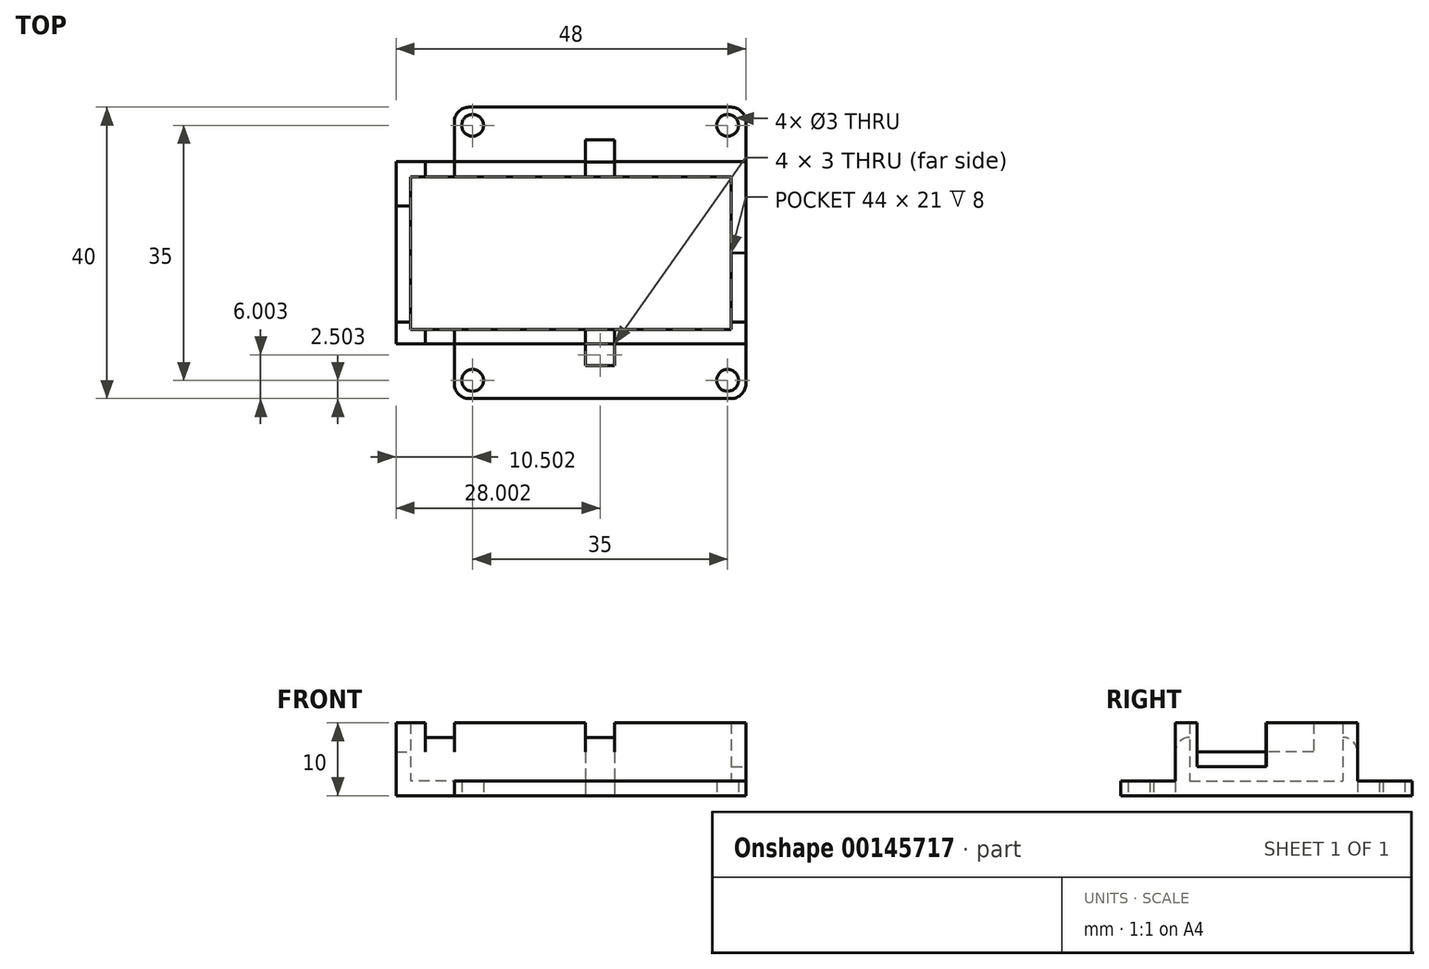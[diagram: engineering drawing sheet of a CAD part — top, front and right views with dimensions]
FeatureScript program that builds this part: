
annotation { "Feature Type Name" : "Feature", "Feature Type Description" : "" }
export const myFeature = defineFeature(function(context is Context, id is Id, definition is map)
    precondition{}
    {
        {
            var Q0;
            Q0=qCreatedBy(makeId("Top.planeOp"),FACE);
            var sketch = newSketch(context, id + "F0", { "sketchPlane" : qUnion([Q0])});
            skLineSegment(sketch, "E0.bottom", {"start": v(0.1, -19.97) * mm, "end": v(-19.9, -19.97) * mm});
            skLineSegment(sketch, "E0.top", {"start": v(0.1, 0.03) * mm, "end": v(-19.9, 0.03) * mm});
            skLineSegment(sketch, "E0.left", {"start": v(0.1, -19.97) * mm, "end": v(0.1, 0.03) * mm});
            skLineSegment(sketch, "E0.right", {"start": v(-19.9, -19.97) * mm, "end": v(-19.9, 0.03) * mm});
            skPoint(sketch, "E1", {"position": v(-17.4, -17.47) * mm});
            skLineSegment(sketch, "E2.bottom", {"start": v(-1.9, -12.47) * mm, "end": v(0.1, -12.47) * mm});
            skLineSegment(sketch, "E2.top", {"start": v(-1.9, -15.47) * mm, "end": v(0.1, -15.47) * mm});
            skLineSegment(sketch, "E2.left", {"start": v(0.1, -12.47) * mm, "end": v(0.1, -15.47) * mm});
            skLineSegment(sketch, "E2.right", {"start": v(-1.9, -12.47) * mm, "end": v(-1.9, -15.47) * mm});
            skSolve(sketch);
        }
        {
            var Q0;
            Q0=makeQuery(id+"F0.imprint","IMPRINT",FACE,{"disambiguationData":[TD([[makeQuery(id+"F0.imprint","IMPRINT",EDGE,{"derivedFrom":sQuery(id+"F0.wireOp",EDGE,"E0.bottom")}),-1.0]])]});
            extrude(context, id + "F1", {"entities" : qUnion([Q0]), "depth" : 2 * mm});
        }
        {
            var Q0;
            Q0=makeQuery(id+"F1.opExtrude","SWEPT_EDGE",EDGE,{"disambiguationData":[OSD([sQuery(id+"F0.wireOp",EDGE,"E0.bottom"),sQuery(id+"F0.wireOp",EDGE,"E0.right")])]});
            fillet(context, id + "F2", {"entities" : qUnion([Q0]), "radius" : 2 * mm, "tangentPropagation" : true, "allowEdgeOverflow" : false});
        }
        {
            var Q0;
            Q0=sQuery(id+"F0.wireOp",VERTEX,"E1");
            var Q1;
            Q1=makeQuery(id+"F1.opExtrude","SWEPT_BODY",BODY,{"disambiguationData":[OSD([sQuery(id+"F0.wireOp",EDGE,"E0.bottom"),sQuery(id+"F0.wireOp",EDGE,"E0.top"),sQuery(id+"F0.wireOp",EDGE,"E0.left"),sQuery(id+"F0.wireOp",EDGE,"E0.right")])]});
            hole(context, id + "F3", {"style" : HoleStyle.SIMPLE, "endStyle" : HoleEndStyle.THROUGH, "oppositeDirection" : true, "holeDiameter" : 3 * mm, "locations" : qUnion([Q0]), "scope" : qUnion([Q1]), "isTappedThrough" : true});
        }
        {
            var Q0;
            Q0=makeQuery(id+"F1.opExtrude","SWEPT_BODY",BODY,{"disambiguationData":[OSD([sQuery(id+"F0.wireOp",EDGE,"E0.bottom"),sQuery(id+"F0.wireOp",EDGE,"E0.top"),sQuery(id+"F0.wireOp",EDGE,"E0.left"),sQuery(id+"F0.wireOp",EDGE,"E0.right")])]});
            var Q1;
            Q1=makeQuery(id+"F1.opExtrude","SWEPT_FACE",FACE,{"disambiguationData":[OSD([sQuery(id+"F0.wireOp",EDGE,"E0.left")])]});
            mirror(context, id + "F4", {"operationType" : NewBodyOperationType.ADD, "entities" : qUnion([Q0]), "mirrorPlane" : qUnion([Q1])});
        }
        {
            var Q0;
            Q0=makeQuery(id+"F1.opExtrude","SWEPT_BODY",BODY,{"disambiguationData":[OSD([sQuery(id+"F0.wireOp",EDGE,"E0.bottom"),sQuery(id+"F0.wireOp",EDGE,"E0.top"),sQuery(id+"F0.wireOp",EDGE,"E0.left"),sQuery(id+"F0.wireOp",EDGE,"E0.right")])]});
            var Q1;
            {var subQ0=makeQuery(id+"F1.opExtrude","SWEPT_FACE",FACE,{"disambiguationData":[OSD([sQuery(id+"F0.wireOp",EDGE,"E0.top")])]});Q1=makeQuery(id+"F4.boolean.opBoolean","MERGE",FACE,{"derivedFrom":[subQ0,makeQuery(id+"F4.opPattern","COPY",FACE,{"derivedFrom":subQ0,"instanceName":"1"})]});}
            mirror(context, id + "F5", {"operationType" : NewBodyOperationType.ADD, "entities" : qUnion([Q0]), "mirrorPlane" : qUnion([Q1])});
        }
        {
            var Q0;
            {var subQ0=makeQuery(id+"F1.opExtrude","CAP_FACE",FACE,{"disambiguationData":[OSD([sQuery(id+"F0.wireOp",EDGE,"E0.bottom"),sQuery(id+"F0.wireOp",EDGE,"E0.top"),sQuery(id+"F0.wireOp",EDGE,"E0.left"),sQuery(id+"F0.wireOp",EDGE,"E0.right")])],"isStart":true});var subQ1=makeQuery(id+"F4.boolean.opBoolean","MERGE",FACE,{"derivedFrom":[subQ0,makeQuery(id+"F4.opPattern","COPY",FACE,{"derivedFrom":subQ0,"instanceName":"1"})]});Q0=makeQuery(id+"F5.boolean.opBoolean","MERGE",FACE,{"derivedFrom":[subQ1,makeQuery(id+"F5.opPattern","COPY",FACE,{"derivedFrom":subQ1,"instanceName":"1"})]});}
            var sketch = newSketch(context, id + "F6", { "sketchPlane" : qUnion([Q0])});
            skLineSegment(sketch, "E3.bottom", {"start": v(20.1, -12.55) * mm, "end": v(-27.9, -12.55) * mm});
            skLineSegment(sketch, "E3.top", {"start": v(20.1, 12.45) * mm, "end": v(-27.9, 12.45) * mm});
            skLineSegment(sketch, "E3.left", {"start": v(20.1, -12.55) * mm, "end": v(20.1, 12.45) * mm});
            skLineSegment(sketch, "E3.right", {"start": v(-27.9, -12.55) * mm, "end": v(-27.9, 12.45) * mm});
            skLineSegment(sketch, "E4.bottom", {"start": v(18.1, -10.5) * mm, "end": v(-25.9, -10.5) * mm});
            skLineSegment(sketch, "E4.top", {"start": v(18.1, 10.5) * mm, "end": v(-25.9, 10.5) * mm});
            skLineSegment(sketch, "E4.left", {"start": v(18.1, -10.5) * mm, "end": v(18.1, 10.5) * mm});
            skLineSegment(sketch, "E4.right", {"start": v(-25.9, -10.5) * mm, "end": v(-25.9, 10.5) * mm});
            skLineSegment(sketch, "E5", {"start": v(-27.9, -6.5) * mm, "end": v(-25.9, -6.5) * mm});
            skLineSegment(sketch, "E6", {"start": v(-27.9, 9.5) * mm, "end": v(-25.9, 9.5) * mm});
            skLineSegment(sketch, "E7", {"start": v(18.1, 0) * mm, "end": v(20.1, -0.05) * mm});
            skLineSegment(sketch, "E8", {"start": v(18.1, 9.5) * mm, "end": v(20.1, 9.5) * mm});
            skLineSegment(sketch, "E9", {"start": v(-1.9, -12.53) * mm, "end": v(-1.9, -10.5) * mm});
            skLineSegment(sketch, "E10", {"start": v(2.1, -12.53) * mm, "end": v(2.1, -10.5) * mm});
            skLineSegment(sketch, "E11", {"start": v(-1.9, 12.47) * mm, "end": v(-1.9, 10.5) * mm});
            skLineSegment(sketch, "E12", {"start": v(2.1, 12.47) * mm, "end": v(2.1, 10.5) * mm});
            skLineSegment(sketch, "E13", {"start": v(-23.9, 12.45) * mm, "end": v(-23.9, 10.5) * mm});
            skLineSegment(sketch, "E14", {"start": v(-23.9, -10.5) * mm, "end": v(-23.9, -12.55) * mm});
            skSolve(sketch);
        }
        {
            var Q0;
            {var subQ0=sQuery(id+"F6.wireOp",EDGE,"E4.right");var subQ3=sQuery(id+"F6.wireOp",EDGE,"E4.bottom");var subQ4=makeQuery(id+"F6.imprint","INTERSECT",VERTEX,{"derivedFrom":[subQ3,subQ0]});Q0=makeQuery(id+"F6.imprint","IMPRINT",FACE,{"disambiguationData":[TD([[makeQuery(id+"F6.imprint","IMPRINT",EDGE,{"disambiguationData":[TD([[subQ4,-1.0]])],"derivedFrom":subQ0}),-1.0]])]});}
            var Q1;
            {var subQ0=sQuery(id+"F6.wireOp",EDGE,"E7");Q1=makeQuery(id+"F6.imprint","IMPRINT",FACE,{"disambiguationData":[TD([[makeQuery(id+"F6.imprint","IMPRINT",EDGE,{"derivedFrom":subQ0}),1.0]])]});}
            var Q2;
            {var subQ7=sQuery(id+"F6.wireOp",EDGE,"E4.bottom");var subQ9=sQuery(id+"F6.wireOp",EDGE,"E4.left");var subQ13=makeQuery(id+"F6.imprint","INTERSECT",VERTEX,{"derivedFrom":[subQ7,subQ9]});Q2=makeQuery(id+"F6.imprint","IMPRINT",FACE,{"disambiguationData":[TD([[makeQuery(id+"F6.imprint","IMPRINT",EDGE,{"disambiguationData":[TD([[subQ13,-1.0]])],"derivedFrom":subQ7}),-1.0]])]});}
            extrude(context, id + "F7", {"entities" : qUnion([Q0, Q1, Q2]), "operationType" : NewBodyOperationType.ADD, "oppositeDirection" : true, "depth" : 2 * mm});
        }
        {
            var Q0;
            {var subQ0=sQuery(id+"F6.wireOp",EDGE,"E13");Q0=makeQuery(id+"F6.imprint","IMPRINT",FACE,{"disambiguationData":[TD([[makeQuery(id+"F6.imprint","IMPRINT",EDGE,{"derivedFrom":subQ0}),1.0]])]});}
            var Q1;
            {var subQ0=sQuery(id+"F6.wireOp",EDGE,"E14");Q1=makeQuery(id+"F6.imprint","IMPRINT",FACE,{"disambiguationData":[TD([[makeQuery(id+"F6.imprint","IMPRINT",EDGE,{"derivedFrom":subQ0}),1.0]])]});}
            var Q2;
            {var subQ0=sQuery(id+"F6.wireOp",EDGE,"E9");Q2=makeQuery(id+"F6.imprint","IMPRINT",FACE,{"disambiguationData":[TD([[makeQuery(id+"F6.imprint","IMPRINT",EDGE,{"derivedFrom":subQ0}),-1.0]])]});}
            var Q3;
            {var subQ0=sQuery(id+"F6.wireOp",EDGE,"E12");var subQ1=sQuery(id+"F6.wireOp",EDGE,"E3.top");var subQ2=makeQuery(id+"F6.imprint","INTERSECT",VERTEX,{"derivedFrom":[subQ1,subQ0]});Q3=makeQuery(id+"F6.imprint","IMPRINT",FACE,{"disambiguationData":[TD([[makeQuery(id+"F6.imprint","IMPRINT",EDGE,{"disambiguationData":[TD([[subQ2,-1.0]])],"derivedFrom":subQ1}),1.0]])]});}
            extrude(context, id + "F8", {"entities" : qUnion([Q0, Q1, Q2, Q3]), "operationType" : NewBodyOperationType.ADD, "oppositeDirection" : true, "depth" : 8 * mm});
        }
        {
            var Q0;
            {var subQ3=sQuery(id+"F6.wireOp",EDGE,"E5");Q0=makeQuery(id+"F6.imprint","IMPRINT",FACE,{"disambiguationData":[TD([[makeQuery(id+"F6.imprint","IMPRINT",EDGE,{"derivedFrom":subQ3}),-1.0]])]});}
            var Q1;
            {var subQ3=sQuery(id+"F6.wireOp",EDGE,"E6");Q1=makeQuery(id+"F6.imprint","IMPRINT",FACE,{"disambiguationData":[TD([[makeQuery(id+"F6.imprint","IMPRINT",EDGE,{"derivedFrom":subQ3}),1.0]])]});}
            var Q2;
            {var subQ0=sQuery(id+"F6.wireOp",EDGE,"E9");var subQ6=sQuery(id+"F6.wireOp",EDGE,"E4.bottom");var subQ7=makeQuery(id+"F6.imprint","INTERSECT",VERTEX,{"derivedFrom":[subQ6,subQ0]});Q2=makeQuery(id+"F6.imprint","IMPRINT",FACE,{"disambiguationData":[TD([[makeQuery(id+"F6.imprint","IMPRINT",EDGE,{"disambiguationData":[TD([[subQ7,1.0]])],"derivedFrom":subQ0}),1.0]])]});}
            var Q3;
            {var subQ3=sQuery(id+"F6.wireOp",EDGE,"E7");Q3=makeQuery(id+"F6.imprint","IMPRINT",FACE,{"disambiguationData":[TD([[makeQuery(id+"F6.imprint","IMPRINT",EDGE,{"derivedFrom":subQ3}),-1.0]])]});}
            var Q4;
            {var subQ3=sQuery(id+"F6.wireOp",EDGE,"E8");Q4=makeQuery(id+"F6.imprint","IMPRINT",FACE,{"disambiguationData":[TD([[makeQuery(id+"F6.imprint","IMPRINT",EDGE,{"derivedFrom":subQ3}),1.0]])]});}
            var Q5;
            {var subQ0=sQuery(id+"F6.wireOp",EDGE,"E11");var subQ6=sQuery(id+"F6.wireOp",EDGE,"E4.top");var subQ7=makeQuery(id+"F6.imprint","INTERSECT",VERTEX,{"derivedFrom":[subQ6,subQ0]});Q5=makeQuery(id+"F6.imprint","IMPRINT",FACE,{"disambiguationData":[TD([[makeQuery(id+"F6.imprint","IMPRINT",EDGE,{"disambiguationData":[TD([[subQ7,1.0]])],"derivedFrom":subQ0}),-1.0]])]});}
            extrude(context, id + "F9", {"entities" : qUnion([Q0, Q1, Q2, Q3, Q4, Q5]), "operationType" : NewBodyOperationType.ADD, "oppositeDirection" : true, "depth" : 10 * mm});
        }
        {
            var Q0;
            Q0=makeQuery(id+"F8.opExtrude","CAP_EDGE",EDGE,{"disambiguationData":[OSD([sQuery(id+"F0.wireOp",EDGE,"E2.bottom")])],"isStart":false});
            var Q1;
            Q1=makeQuery(id+"F8.opExtrude","CAP_EDGE",EDGE,{"disambiguationData":[OSD([sQuery(id+"F6.wireOp",EDGE,"E3.bottom")])],"isStart":false});
            var Q2;
            Q2=makeQuery(id+"F8.opExtrude","CAP_EDGE",EDGE,{"disambiguationData":[OSD([sQuery(id+"F6.wireOp",EDGE,"E3.top")])],"isStart":false});
            fillet(context, id + "F10", {"entities" : qUnion([Q0, Q1, Q2]), "radius" : 2 * mm, "tangentPropagation" : true, "allowEdgeOverflow" : false});
        }
        {
            var Q0;
            {var subQ0=sQuery(id+"F6.wireOp",EDGE,"E7");Q0=makeQuery(id+"F6.imprint","IMPRINT",FACE,{"disambiguationData":[TD([[makeQuery(id+"F6.imprint","IMPRINT",EDGE,{"derivedFrom":subQ0}),1.0]])]});}
            extrude(context, id + "F11", {"entities" : qUnion([Q0]), "operationType" : NewBodyOperationType.ADD, "oppositeDirection" : true, "depth" : 4 * mm});
        }
        {
            var Q0;
            {var subQ0=sQuery(id+"F6.wireOp",EDGE,"E5");Q0=makeQuery(id+"F6.imprint","IMPRINT",FACE,{"disambiguationData":[TD([[makeQuery(id+"F6.imprint","IMPRINT",EDGE,{"derivedFrom":subQ0}),1.0]])]});}
            extrude(context, id + "F12", {"entities" : qUnion([Q0]), "operationType" : NewBodyOperationType.ADD, "oppositeDirection" : true, "depth" : 6 * mm});
        }
    });
